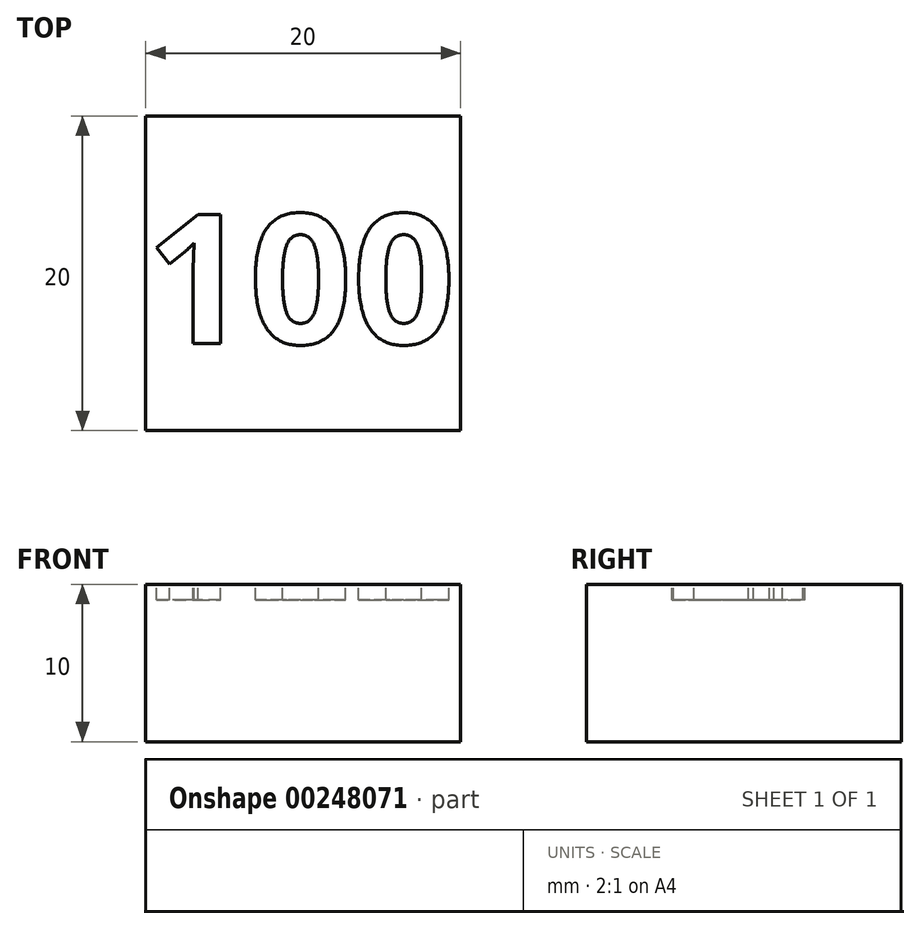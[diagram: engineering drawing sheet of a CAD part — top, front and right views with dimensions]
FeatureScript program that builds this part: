
annotation { "Feature Type Name" : "Feature", "Feature Type Description" : "" }
export const myFeature = defineFeature(function(context is Context, id is Id, definition is map)
    precondition{}
    {
        {
            var Q0;
            Q0=qCreatedBy(makeId("Top.planeOp"),FACE);
            var sketch = newSketch(context, id + "F0", { "sketchPlane" : qUnion([Q0])});
            skLineSegment(sketch, "E0.bottom", {"start": v(0, 0) * mm, "end": v(20, 0) * mm});
            skLineSegment(sketch, "E0.top", {"start": v(0, 20) * mm, "end": v(20, 20) * mm});
            skLineSegment(sketch, "E0.left", {"start": v(0, 0) * mm, "end": v(0, 20) * mm});
            skLineSegment(sketch, "E0.right", {"start": v(20, 0) * mm, "end": v(20, 20) * mm});
            skSolve(sketch);
        }
        {
            var Q0;
            Q0 = qSketchRegion(id + "F0", true);
            extrude(context, id + "F1", {"entities" : qUnion([Q0]), "depth" : 10 * mm});
        }
        {
            var Q0;
            Q0=makeQuery(id+"F1.opExtrude","CAP_FACE",FACE,{"disambiguationData":[OSD([sQuery(id+"F0.wireOp",EDGE,"E0.bottom"),sQuery(id+"F0.wireOp",EDGE,"E0.top"),sQuery(id+"F0.wireOp",EDGE,"E0.left"),sQuery(id+"F0.wireOp",EDGE,"E0.right")])],"isStart":false});
            var sketch = newSketch(context, id + "F2", { "sketchPlane" : qUnion([Q0])});
            skText(sketch, "E1", { "text": "100", "fontName": "OpenSans-Bold.ttf"});
            const initialGuessF2  = {"E1": [0, 0.00553, 1, 0, 0.00827]};
            skSetInitialGuess(sketch, initialGuessF2);
            skSolve(sketch);
        }
        {
            var Q0;
            Q0 = qSketchRegion(id + "F2", true);
            extrude(context, id + "F3", {"entities" : qUnion([Q0]), "operationType" : NewBodyOperationType.REMOVE, "oppositeDirection" : true, "depth" : 1 * mm});
        }
    });
